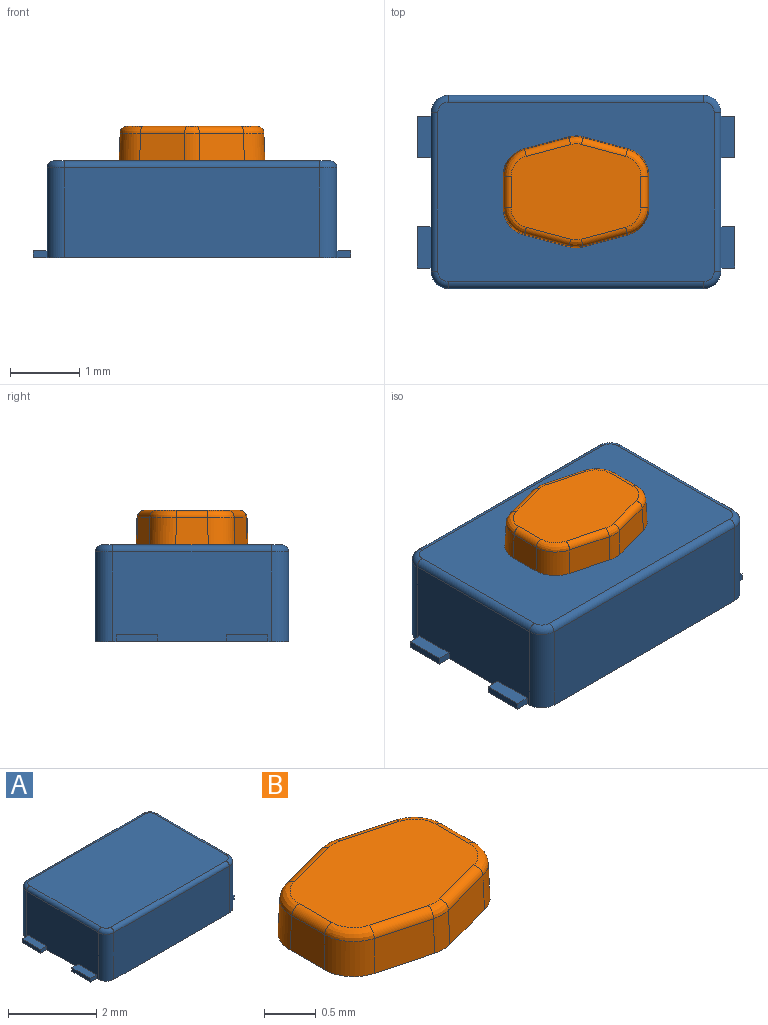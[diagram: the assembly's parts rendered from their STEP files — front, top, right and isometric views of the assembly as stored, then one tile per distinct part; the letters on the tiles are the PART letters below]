
ASSEMBLY  parts=2 mates=1
PART A: 34 faces, bbox 4.6x2.8x1.4 mm
  f0: plane 2.3x1.3mm, normal (1,0,0), area 2.9mm2, adj f5,f7,f8,f12,f26,f28,f29,f30
  f1: plane 2.3x1.3mm, normal (-1,0,0), area 2.9mm2, adj f5,f6,f9,f15,f18,f20,f21,f22
  f2: plane 3.7x1.3mm, normal (0,1,0), area 4.8mm2, adj f5,f6,f7,f11
  f3: plane 3.7x1.3mm, normal (0,-1,0), area 4.8mm2, adj f5,f8,f9,f16
  f4: plane 4x2.6mm, normal (0,0,1), area 10.4mm2, adj f10,f11,f12,f13,f14,f15,f16,f17
  f5: plane 4.6x2.8mm, normal (0,0,-1), area 12.2mm2, adj f0,f1,f2,f3,f6,f7,f8,f9
  f6: cylinder r=0.25mm len=1.3mm, axis (0,0,-1), area 0.5mm2, adj f1,f2,f5,f13
  f7: cylinder r=0.25mm len=1.3mm, axis (0,0,-1), area 0.5mm2, adj f0,f2,f5,f10
  f8: cylinder r=0.25mm len=1.3mm, axis (0,0,-1), area 0.5mm2, adj f0,f3,f5,f14
  f9: cylinder r=0.25mm len=1.3mm, axis (0,0,-1), area 0.5mm2, adj f1,f3,f5,f17
  f10: torus R=0.15mm, axis (0,0,1), area 0.1mm2, adj f4,f7,f11,f12
  f11: cylinder r=0.1mm len=3.7mm, axis (1,0,0), area 0.6mm2, adj f2,f4,f10,f13
  f12: cylinder r=0.1mm len=2.3mm, axis (0,-1,0), area 0.4mm2, adj f0,f4,f10,f14
  f13: torus R=0.15mm, axis (0,0,1), area 0.1mm2, adj f4,f6,f11,f15
  f14: torus R=0.15mm, axis (0,0,1), area 0.1mm2, adj f4,f8,f12,f16
  f15: cylinder r=0.1mm len=2.3mm, axis (0,1,0), area 0.4mm2, adj f1,f4,f13,f17
  f16: cylinder r=0.1mm len=3.7mm, axis (-1,0,0), area 0.6mm2, adj f3,f4,f14,f17
  f17: torus R=0.15mm, axis (0,0,1), area 0.1mm2, adj f4,f9,f15,f16
  f18: plane 0.2x0.1mm, normal (0,1,0), area 0mm2, adj f1,f5,f19,f21
  f19: plane 0.6x0.1mm, normal (-1,0,0), area 0.1mm2, adj f5,f18,f20,f21
  f20: plane 0.2x0.1mm, normal (0,-1,0), area 0mm2, adj f1,f5,f19,f21
  f21: plane 0.6x0.2mm, normal (0,0,1), area 0.1mm2, adj f1,f18,f19,f20
  f22: plane 0.2x0.1mm, normal (0,-1,0), area 0mm2, adj f1,f5,f24,f25
  f23: plane 0.2x0.1mm, normal (0,1,0), area 0mm2, adj f1,f5,f24,f25
  f24: plane 0.6x0.1mm, normal (-1,0,0), area 0.1mm2, adj f5,f22,f23,f25
  f25: plane 0.6x0.2mm, normal (0,0,1), area 0.1mm2, adj f1,f22,f23,f24
  f26: plane 0.2x0.1mm, normal (0,-1,0), area 0mm2, adj f0,f5,f27,f29
  f27: plane 0.6x0.1mm, normal (1,0,0), area 0.1mm2, adj f5,f26,f28,f29
  f28: plane 0.2x0.1mm, normal (0,1,0), area 0mm2, adj f0,f5,f27,f29
  f29: plane 0.6x0.2mm, normal (0,0,1), area 0.1mm2, adj f0,f26,f27,f28
  f30: plane 0.2x0.1mm, normal (0,1,0), area 0mm2, adj f0,f5,f32,f33
  f31: plane 0.2x0.1mm, normal (0,-1,0), area 0mm2, adj f0,f5,f32,f33
  f32: plane 0.6x0.1mm, normal (1,0,0), area 0.1mm2, adj f5,f30,f31,f33
  f33: plane 0.6x0.2mm, normal (0,0,1), area 0.1mm2, adj f0,f30,f31,f32
PART B: 26 faces, bbox 2.1x1.6x0.5 mm
  f0: plane 0.66x0.4mm, normal (-0.26,0.97,0.03), area 0.3mm2, adj f7,f8,f9,f24
  f1: plane 0.47x0.4mm, normal (-1,0,0.03), area 0.2mm2, adj f7,f8,f13,f20
  f2: plane 0.66x0.4mm, normal (-0.26,-0.97,0.03), area 0.3mm2, adj f7,f12,f13,f16
  f3: plane 0.66x0.4mm, normal (0.26,-0.97,0.03), area 0.3mm2, adj f7,f11,f12,f15
  f4: plane 0.47x0.4mm, normal (1,0,0.03), area 0.2mm2, adj f7,f10,f11,f19
  f5: plane 0.66x0.4mm, normal (0.26,0.97,0.03), area 0.3mm2, adj f7,f9,f10,f23
  f6: plane 1.89x1.4mm, normal (0,0,1), area 2.1mm2, adj f14,f15,f16,f17,f18,f19,f20,f21
  f7: plane 2.12x1.63mm, normal (0,0,-1), area 2.8mm2, adj f0,f1,f2,f3,f4,f5,f8,f9
  f8: cylinder r=0.4mm len=0.41mm, axis (-0.03,0.03,-1), area 0.2mm2, adj f0,f1,f7,f22
  f9: cylinder r=0.4mm len=0.4mm, axis (0,0.04,-1), area 0.1mm2, adj f0,f5,f7,f25
  f10: cylinder r=0.4mm len=0.41mm, axis (0.03,0.03,-1), area 0.2mm2, adj f4,f5,f7,f21
  f11: cylinder r=0.4mm len=0.41mm, axis (0.03,-0.03,-1), area 0.2mm2, adj f3,f4,f7,f17
  f12: cylinder r=0.4mm len=0.4mm, axis (0,-0.04,-1), area 0.1mm2, adj f2,f3,f7,f14
  f13: cylinder r=0.4mm len=0.41mm, axis (-0.03,-0.03,-1), area 0.2mm2, adj f1,f2,f7,f18
  f14: bspline ~0.21x0.11mm, area 0mm2, adj f6,f12,f15,f16
  f15: cylinder r=0.1mm len=0.67mm, axis (0.97,0.26,0), area 0.1mm2, adj f3,f6,f14,f17
  f16: cylinder r=0.1mm len=0.67mm, axis (0.97,-0.26,0), area 0.1mm2, adj f2,f6,f14,f18
  f17: bspline ~0.39x0.32mm, area 0.1mm2, adj f6,f11,f15,f19
  f18: bspline ~0.39x0.32mm, area 0.1mm2, adj f6,f13,f16,f20
  f19: cylinder r=0.1mm len=0.45mm, axis (0,1,0), area 0.1mm2, adj f4,f6,f17,f21
  f20: cylinder r=0.1mm len=0.45mm, axis (0,-1,0), area 0.1mm2, adj f1,f6,f18,f22
  f21: bspline ~0.39x0.32mm, area 0.1mm2, adj f6,f10,f19,f23
  f22: bspline ~0.39x0.32mm, area 0.1mm2, adj f6,f8,f20,f24
  f23: cylinder r=0.1mm len=0.67mm, axis (-0.97,0.26,0), area 0.1mm2, adj f5,f6,f21,f25
  f24: cylinder r=0.1mm len=0.67mm, axis (-0.97,-0.26,0), area 0.1mm2, adj f0,f6,f22,f25
  f25: bspline ~0.21x0.11mm, area 0mm2, adj f6,f9,f23,f24
PLACE A t=(0,0,-0.88)mm
PLACE B t=(0,0,-0.88)mm
MATE fastened B.f7 <-> A.f4  axis (0,0,-1) through (0,0,-0.18)mm
